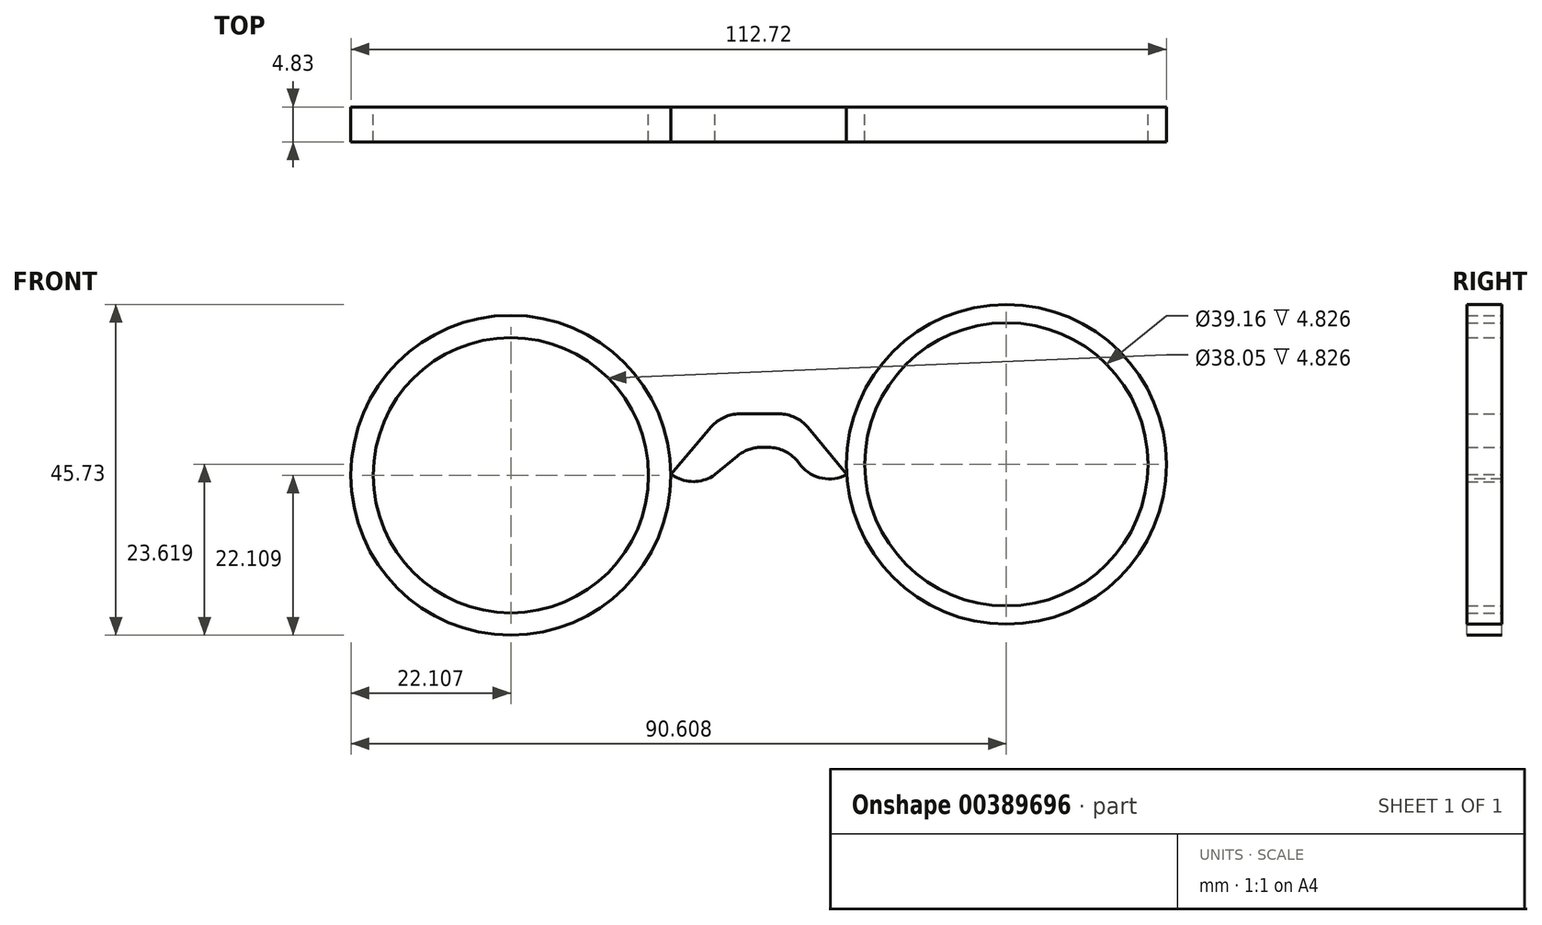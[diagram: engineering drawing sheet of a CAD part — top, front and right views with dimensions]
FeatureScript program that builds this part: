
annotation { "Feature Type Name" : "Feature", "Feature Type Description" : "" }
export const myFeature = defineFeature(function(context is Context, id is Id, definition is map)
    precondition{}
    {
        {
            var Q0;
            Q0=qCreatedBy(makeId("Front.planeOp"),FACE);
            var sketch = newSketch(context, id + "F0", { "sketchPlane" : qUnion([Q0])});
            skCircle(sketch, "E0", {"center": v(35.74, 4.29) * mm, "radius": 22.11 * mm});
            skCircle(sketch, "E1", {"center": v(-32.76, 2.78) * mm, "radius": 22.11 * mm});
            skLineSegment(sketch, "E2", {"start": v(13.67, 2.88) * mm, "end": v(6.74, 11.26) * mm});
            skLineSegment(sketch, "E3", {"start": v(6.74, 11.26) * mm, "end": v(-3.51, 11.26) * mm});
            skLineSegment(sketch, "E4", {"start": v(-3.51, 11.26) * mm, "end": v(-10.65, 2.88) * mm});
            skLineSegment(sketch, "E5", {"start": v(-10.65, 2.88) * mm, "end": v(-7.08, 1.08) * mm});
            skPoint(sketch, "E5.endSnap0", {"position": v(-7.08, 7.07) * mm});
            skLineSegment(sketch, "E6", {"start": v(-7.08, 1.08) * mm, "end": v(-4.54, 2.88) * mm});
            skLineSegment(sketch, "E7", {"start": v(-4.54, 2.88) * mm, "end": v(0, 6.63) * mm});
            skLineSegment(sketch, "E8", {"start": v(0, 6.63) * mm, "end": v(5.27, 6.63) * mm});
            skLineSegment(sketch, "E9", {"start": v(5.27, 6.63) * mm, "end": v(10.75, 0) * mm});
            skLineSegment(sketch, "E10", {"start": v(10.75, 0) * mm, "end": v(13.67, 2.88) * mm});
            skCircle(sketch, "E11", {"center": v(-32.76, 2.78) * mm, "radius": 19.03 * mm});
            skCircle(sketch, "E12", {"center": v(35.74, 4.29) * mm, "radius": 19.58 * mm});
            skSolve(sketch);
        }
        {
            var Q0;
            Q0 = qSketchRegion(id + "F0", true);
            extrude(context, id + "F1", {"entities" : qUnion([Q0]), "depth" : 4.83 * mm});
        }
        {
            var Q0;
            Q0=makeQuery(id+"F1.opExtrude","SWEPT_EDGE",EDGE,{"disambiguationData":[OSD([sQuery(id+"F0.wireOp",EDGE,"E2"),sQuery(id+"F0.wireOp",EDGE,"E3")])]});
            var Q1;
            Q1=makeQuery(id+"F1.opExtrude","SWEPT_EDGE",EDGE,{"disambiguationData":[OSD([sQuery(id+"F0.wireOp",EDGE,"E3"),sQuery(id+"F0.wireOp",EDGE,"E4")])]});
            var Q2;
            Q2=makeQuery(id+"F1.opExtrude","SWEPT_EDGE",EDGE,{"disambiguationData":[OSD([sQuery(id+"F0.wireOp",EDGE,"E8"),sQuery(id+"F0.wireOp",EDGE,"E9")])]});
            var Q3;
            Q3=makeQuery(id+"F1.opExtrude","SWEPT_EDGE",EDGE,{"disambiguationData":[OSD([sQuery(id+"F0.wireOp",EDGE,"E7"),sQuery(id+"F0.wireOp",EDGE,"E8")])]});
            var Q4;
            Q4=makeQuery(id+"F1.opExtrude","SWEPT_EDGE",EDGE,{"disambiguationData":[OSD([sQuery(id+"F0.wireOp",EDGE,"E9"),sQuery(id+"F0.wireOp",EDGE,"E10")])]});
            var Q5;
            Q5=makeQuery(id+"F1.opExtrude","SWEPT_EDGE",EDGE,{"disambiguationData":[OSD([sQuery(id+"F0.wireOp",EDGE,"E5"),sQuery(id+"F0.wireOp",EDGE,"E6")])]});
            fillet(context, id + "F2", {"entities" : qUnion([Q0, Q1, Q2, Q3, Q4, Q5]), "radius" : 5.08 * mm, "tangentPropagation" : true, "allowEdgeOverflow" : false});
        }
    });
